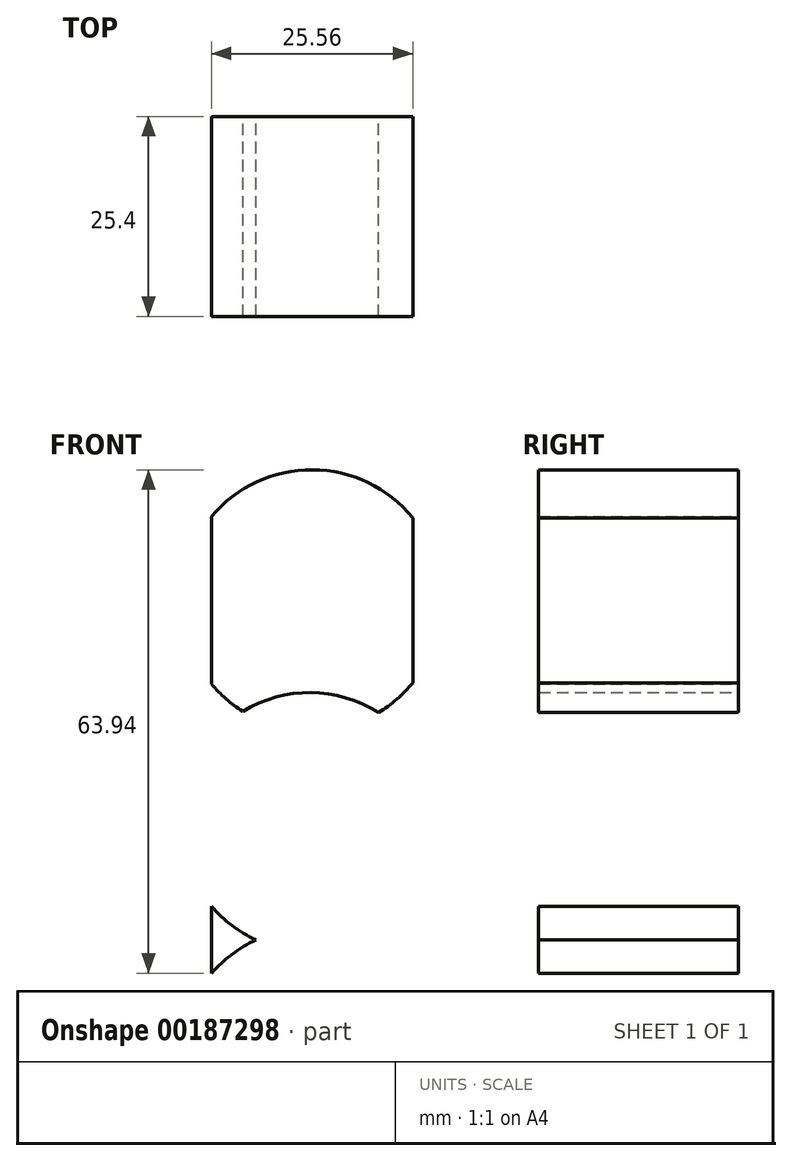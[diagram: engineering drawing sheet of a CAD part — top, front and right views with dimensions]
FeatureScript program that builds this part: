
annotation { "Feature Type Name" : "Feature", "Feature Type Description" : "" }
export const myFeature = defineFeature(function(context is Context, id is Id, definition is map)
    precondition{}
    {
        {
            var Q0;
            Q0=qCreatedBy(makeId("Front.planeOp"),FACE);
            var sketch = newSketch(context, id + "F0", { "sketchPlane" : qUnion([Q0])});
            skLineSegment(sketch, "E0", {"start": v(-22.58, 62.23) * mm, "end": v(-22.58, -27.84) * mm});
            skLineSegment(sketch, "E1", {"start": v(2.98, 62.36) * mm, "end": v(2.98, -27.84) * mm});
            skCircle(sketch, "E2", {"center": v(-9.86, 45.36) * mm, "radius": 16.58 * mm});
            skCircle(sketch, "E3", {"center": v(-10.12, 17.2) * mm, "radius": 16.44 * mm});
            skCircle(sketch, "E4", {"center": v(-9.08, -14.08) * mm, "radius": 18.11 * mm});
            skSolve(sketch);
        }
        {
            var Q0;
            {var subQ0=sQuery(id+"F0.wireOp",EDGE,"E3");var subQ7=sQuery(id+"F0.wireOp",EDGE,"E0");var subQ8=makeQuery(id+"F0.imprint","INTERSECT",VERTEX,{"disambiguationData":[OD(0.0)],"derivedFrom":[subQ7,subQ0]});Q0=makeQuery(id+"F0.imprint","IMPRINT",FACE,{"disambiguationData":[TD([[makeQuery(id+"F0.imprint","IMPRINT",EDGE,{"disambiguationData":[TD([[subQ8,-1.0]])],"derivedFrom":subQ7}),1.0]])]});}
            var Q1;
            {var subQ0=sQuery(id+"F0.wireOp",EDGE,"E2");var subQ1=sQuery(id+"F0.wireOp",EDGE,"E0");var subQ8=makeQuery(id+"F0.imprint","INTERSECT",VERTEX,{"disambiguationData":[OD(0.0)],"derivedFrom":[subQ1,subQ0]});Q1=makeQuery(id+"F0.imprint","IMPRINT",FACE,{"disambiguationData":[TD([[makeQuery(id+"F0.imprint","IMPRINT",EDGE,{"disambiguationData":[TD([[subQ8,-1.0]])],"derivedFrom":subQ1}),1.0]])]});}
            var Q2;
            {var subQ0=sQuery(id+"F0.wireOp",EDGE,"E4");var subQ7=sQuery(id+"F0.wireOp",EDGE,"E0");var subQ8=makeQuery(id+"F0.imprint","INTERSECT",VERTEX,{"disambiguationData":[OD(0.0)],"derivedFrom":[subQ7,subQ0]});Q2=makeQuery(id+"F0.imprint","IMPRINT",FACE,{"disambiguationData":[TD([[makeQuery(id+"F0.imprint","IMPRINT",EDGE,{"disambiguationData":[TD([[subQ8,1.0]])],"derivedFrom":subQ7}),1.0]])]});}
            extrude(context, id + "F1", {"entities" : qUnion([Q0, Q1, Q2]), "depth" : 25.4 * mm});
        }
    });
